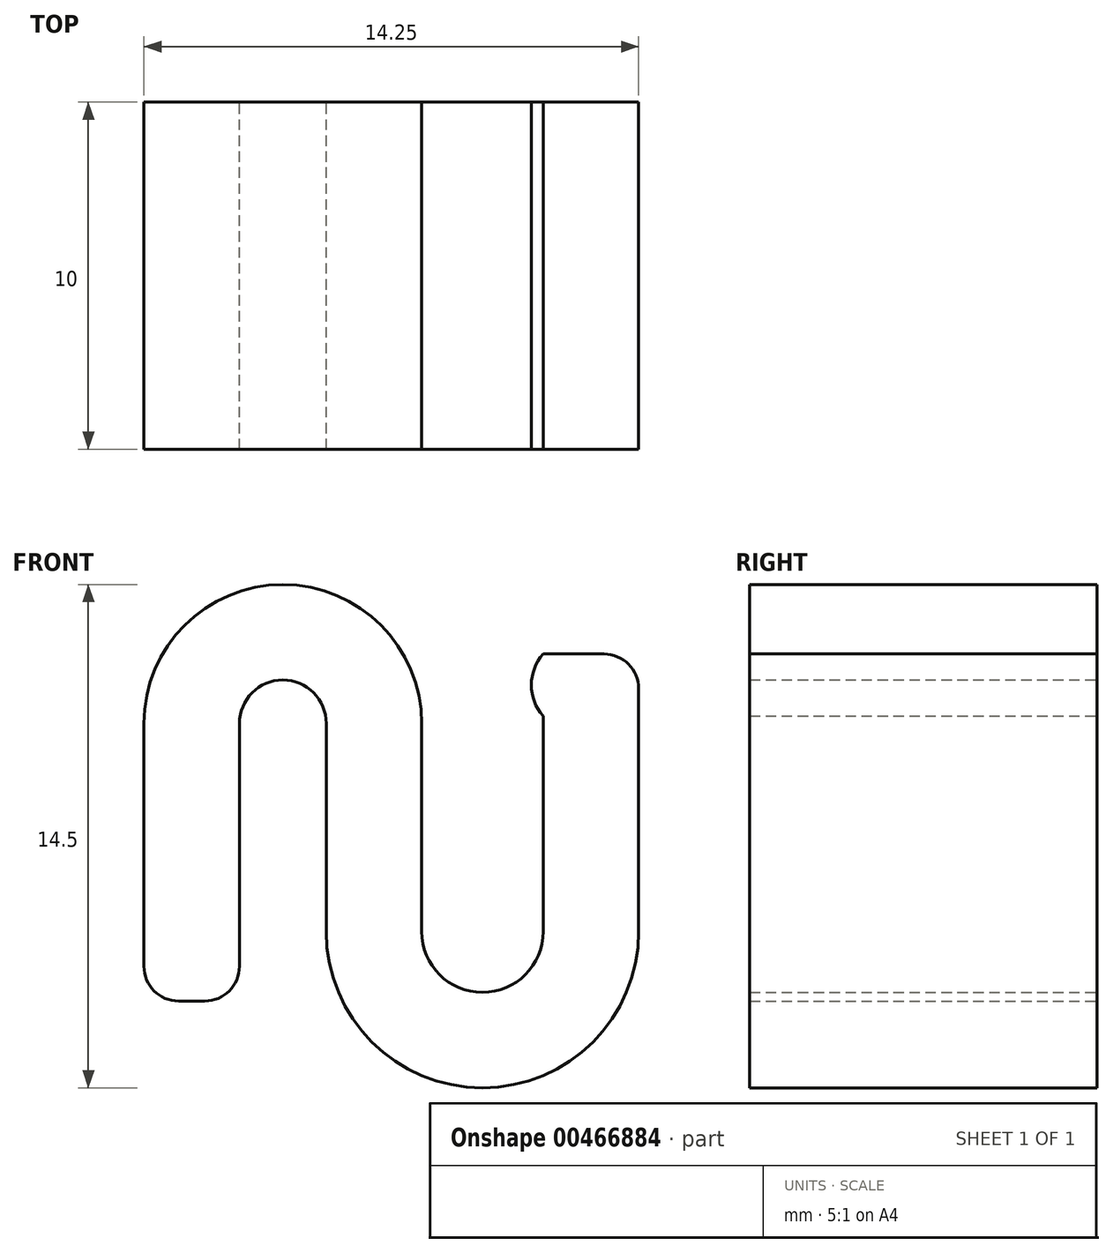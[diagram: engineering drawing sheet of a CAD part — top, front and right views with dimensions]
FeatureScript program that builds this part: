
annotation { "Feature Type Name" : "Feature", "Feature Type Description" : "" }
export const myFeature = defineFeature(function(context is Context, id is Id, definition is map)
    precondition{}
    {
        {
            var Q0;
            Q0=qCreatedBy(makeId("Front.planeOp"),FACE);
            var sketch = newSketch(context, id + "F0", { "sketchPlane" : qUnion([Q0])});
            skCircle(sketch, "E0", {"center": v(-1.25, 3) * mm, "radius": 1.25 * mm});
            skCircle(sketch, "E1", {"center": v(4.5, -3) * mm, "radius": 1.75 * mm});
            skCircle(sketch, "E2", {"center": v(4.5, -3) * mm, "radius": 4.5 * mm});
            skCircle(sketch, "E3", {"center": v(-1.25, 3) * mm, "radius": 4 * mm});
            skLineSegment(sketch, "E4", {"start": v(0, 3) * mm, "end": v(0, -5.38) * mm});
            skLineSegment(sketch, "E5", {"start": v(2.75, 3) * mm, "end": v(2.75, -3) * mm});
            skLineSegment(sketch, "E6", {"start": v(-5.25, 3) * mm, "end": v(-5.25, -5) * mm});
            skLineSegment(sketch, "E7", {"start": v(-5.25, -5) * mm, "end": v(-2.5, -5) * mm});
            skLineSegment(sketch, "E8", {"start": v(-2.5, -5) * mm, "end": v(-2.5, 3) * mm});
            skLineSegment(sketch, "E9", {"start": v(6.25, -3) * mm, "end": v(6.25, 5) * mm});
            skLineSegment(sketch, "E10", {"start": v(6.25, 5) * mm, "end": v(9, 5) * mm});
            skLineSegment(sketch, "E11", {"start": v(9, 5) * mm, "end": v(9, -3) * mm});
            skCircle(sketch, "E12", {"center": v(7.25, 4.1) * mm, "radius": 1.34 * mm});
            skSolve(sketch);
        }
        {
            var Q0;
            {var subQ0=sQuery(id+"F0.wireOp",EDGE,"E6");Q0=makeQuery(id+"F0.imprint","IMPRINT",FACE,{"disambiguationData":[TD([[makeQuery(id+"F0.imprint","IMPRINT",EDGE,{"derivedFrom":subQ0}),1.0]])]});}
            var Q1;
            {var subQ4=sQuery(id+"F0.wireOp",EDGE,"E4");var subQ5=sQuery(id+"F0.wireOp",EDGE,"E0");var subQ6=makeQuery(id+"F0.imprint","INTERSECT",VERTEX,{"derivedFrom":[subQ5,subQ4]});Q1=makeQuery(id+"F0.imprint","IMPRINT",FACE,{"disambiguationData":[TD([[makeQuery(id+"F0.imprint","IMPRINT",EDGE,{"disambiguationData":[TD([[subQ6,-1.0]])],"derivedFrom":subQ5}),-1.0]])]});}
            var Q2;
            {var subQ0=sQuery(id+"F0.wireOp",EDGE,"E5");var subQ10=sQuery(id+"F0.wireOp",EDGE,"E1");var subQ11=makeQuery(id+"F0.imprint","INTERSECT",VERTEX,{"derivedFrom":[subQ10,subQ0]});Q2=makeQuery(id+"F0.imprint","IMPRINT",FACE,{"disambiguationData":[TD([[makeQuery(id+"F0.imprint","IMPRINT",EDGE,{"disambiguationData":[TD([[subQ11,-1.0]])],"derivedFrom":subQ10}),-1.0]])]});}
            var Q3;
            {var subQ4=sQuery(id+"F0.wireOp",EDGE,"E10");Q3=makeQuery(id+"F0.imprint","IMPRINT",FACE,{"disambiguationData":[TD([[makeQuery(id+"F0.imprint","IMPRINT",EDGE,{"derivedFrom":subQ4}),-1.0]])]});}
            var Q4;
            {var subQ0=sQuery(id+"F0.wireOp",EDGE,"E5");var subQ1=sQuery(id+"F0.wireOp",EDGE,"E2");var subQ2=makeQuery(id+"F0.imprint","INTERSECT",VERTEX,{"derivedFrom":[subQ1,subQ0]});Q4=makeQuery(id+"F0.imprint","IMPRINT",FACE,{"disambiguationData":[TD([[makeQuery(id+"F0.imprint","IMPRINT",EDGE,{"disambiguationData":[TD([[subQ2,-1.0]])],"derivedFrom":subQ1}),-1.0]])]});}
            var Q5;
            {var subQ0=sQuery(id+"F0.wireOp",EDGE,"E3");var subQ1=sQuery(id+"F0.wireOp",EDGE,"E2");var subQ2=makeQuery(id+"F0.imprint","INTERSECT",VERTEX,{"disambiguationData":[OD(0.0)],"derivedFrom":[subQ1,subQ0]});Q5=makeQuery(id+"F0.imprint","IMPRINT",FACE,{"disambiguationData":[TD([[makeQuery(id+"F0.imprint","IMPRINT",EDGE,{"disambiguationData":[TD([[subQ2,-1.0]])],"derivedFrom":subQ1}),1.0]])]});}
            var Q6;
            {var subQ0=sQuery(id+"F0.wireOp",EDGE,"E4");var subQ1=sQuery(id+"F0.wireOp",EDGE,"E2");var subQ2=makeQuery(id+"F0.imprint","INTERSECT",VERTEX,{"derivedFrom":[subQ1,subQ0]});Q6=makeQuery(id+"F0.imprint","IMPRINT",FACE,{"disambiguationData":[TD([[makeQuery(id+"F0.imprint","IMPRINT",EDGE,{"disambiguationData":[TD([[subQ2,1.0]])],"derivedFrom":subQ1}),-1.0]])]});}
            var Q7;
            {var subQ0=sQuery(id+"F0.wireOp",EDGE,"E11");Q7=makeQuery(id+"F0.imprint","IMPRINT",FACE,{"disambiguationData":[TD([[makeQuery(id+"F0.imprint","IMPRINT",EDGE,{"derivedFrom":subQ0}),-1.0]])]});}
            var Q8;
            {var subQ0=sQuery(id+"F0.wireOp",EDGE,"E12");var subQ1=sQuery(id+"F0.wireOp",EDGE,"E9");var subQ3=makeQuery(id+"F0.imprint","INTERSECT",VERTEX,{"derivedFrom":[subQ1,subQ0]});Q8=makeQuery(id+"F0.imprint","IMPRINT",FACE,{"disambiguationData":[TD([[makeQuery(id+"F0.imprint","IMPRINT",EDGE,{"disambiguationData":[TD([[subQ3,-1.0]])],"derivedFrom":subQ1}),1.0]])]});}
            extrude(context, id + "F1", {"entities" : qUnion([Q0, Q1, Q2, Q3, Q4, Q5, Q6, Q7, Q8]), "depth" : 10 * mm});
        }
        {
            var Q0;
            Q0=makeQuery(id+"F1.opExtrude","SWEPT_EDGE",EDGE,{"disambiguationData":[OSD([sQuery(id+"F0.wireOp",EDGE,"E7"),sQuery(id+"F0.wireOp",EDGE,"E8")])]});
            var Q1;
            Q1=makeQuery(id+"F1.opExtrude","SWEPT_EDGE",EDGE,{"disambiguationData":[OSD([sQuery(id+"F0.wireOp",EDGE,"E6"),sQuery(id+"F0.wireOp",EDGE,"E7")])]});
            var Q2;
            Q2=makeQuery(id+"F1.opExtrude","SWEPT_EDGE",EDGE,{"disambiguationData":[OSD([sQuery(id+"F0.wireOp",EDGE,"E10"),sQuery(id+"F0.wireOp",EDGE,"E11")])]});
            fillet(context, id + "F2", {"entities" : qUnion([Q0, Q1, Q2]), "radius" : 1 * mm, "tangentPropagation" : true, "allowEdgeOverflow" : false});
        }
    });
